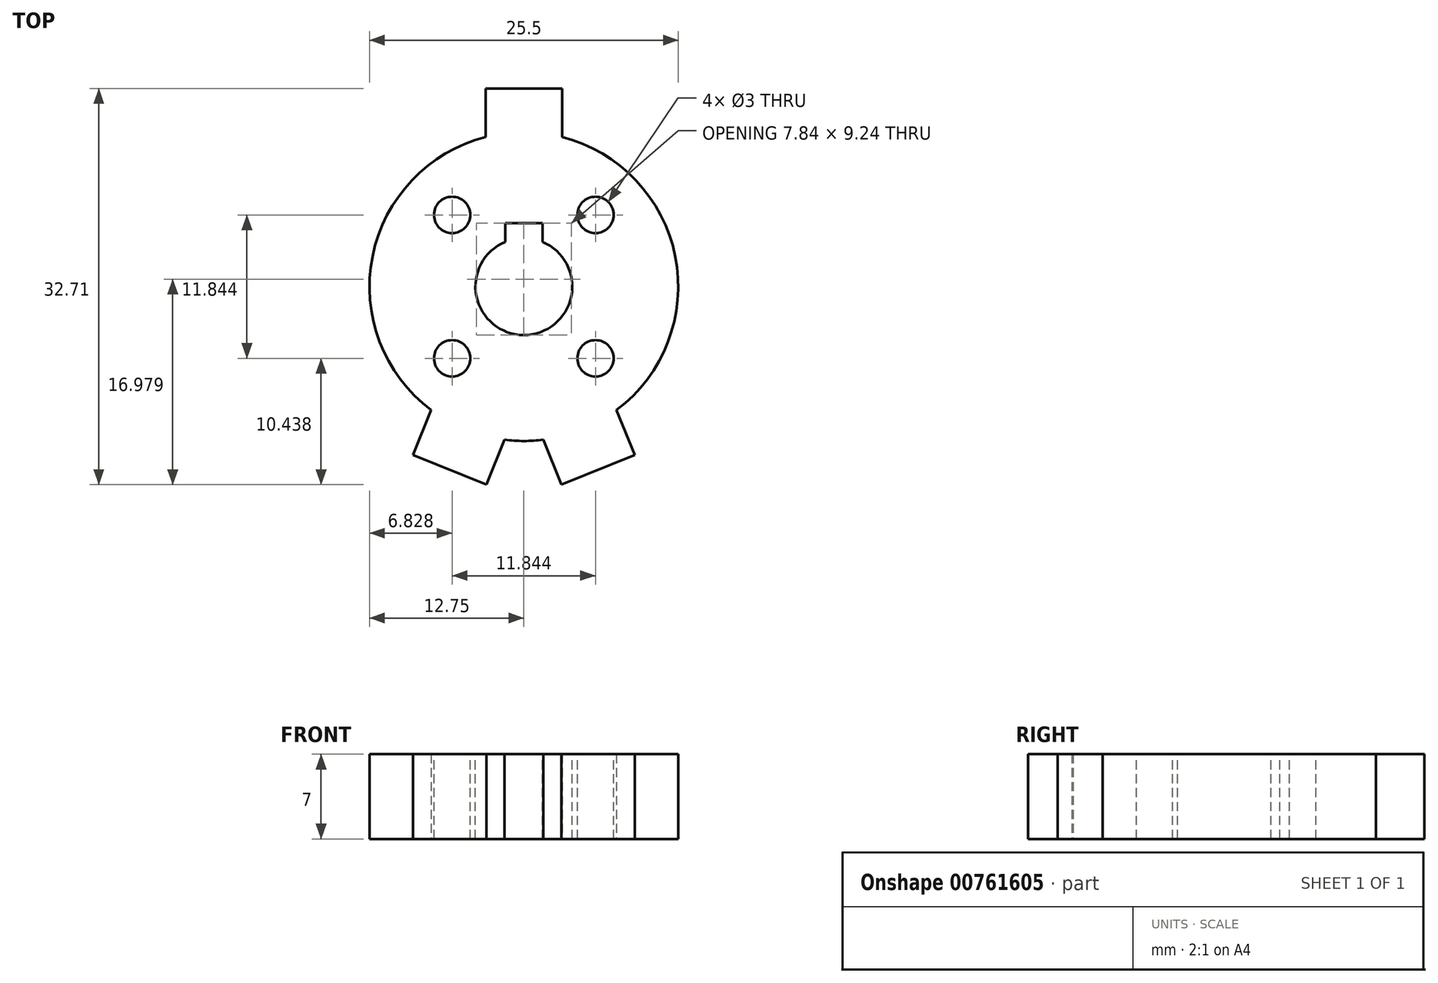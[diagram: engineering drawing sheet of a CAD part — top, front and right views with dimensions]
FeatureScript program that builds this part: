
annotation { "Feature Type Name" : "Feature", "Feature Type Description" : "" }
export const myFeature = defineFeature(function(context is Context, id is Id, definition is map)
    precondition{}
    {
        {
            var Q0;
            Q0=qCreatedBy(makeId("Top.planeOp"),FACE);
            var sketch = newSketch(context, id + "F0", { "sketchPlane" : qUnion([Q0])});
            skArc(sketch, "E0", {"start": v(7.65, -10.2) * mm, "mid": v(12.5, 2.5) * mm, "end": v(3.15, 12.35) * mm});
            skLineSegment(sketch, "E1", {"start": v(0, 12.75) * mm, "end": v(0, -12.75) * mm, "construction": true});
            skLineSegment(sketch, "E2", {"start": v(-3.15, 16.35) * mm, "end": v(0, 16.35) * mm});
            skLineSegment(sketch, "E3", {"start": v(0, 16.35) * mm, "end": v(3.15, 16.35) * mm});
            skLineSegment(sketch, "E4", {"start": v(-3.15, 16.35) * mm, "end": v(-3.15, 12.35) * mm});
            skLineSegment(sketch, "E5", {"start": v(3.15, 16.35) * mm, "end": v(3.15, 12.35) * mm});
            skLineSegment(sketch, "E6", {"start": v(1.6, -12.65) * mm, "end": v(7.65, -10.2) * mm, "construction": true});
            skLineSegment(sketch, "E7", {"start": v(1.6, -12.65) * mm, "end": v(3.1, -16.36) * mm});
            skLineSegment(sketch, "E8", {"start": v(7.65, -10.2) * mm, "end": v(9.15, -13.9) * mm});
            skLineSegment(sketch, "E9", {"start": v(3.1, -16.36) * mm, "end": v(9.15, -13.9) * mm});
            skLineSegment(sketch, "E10.MirrorCS", {"start": v(-1.6, -12.65) * mm, "end": v(-3.1, -16.36) * mm});
            skLineSegment(sketch, "E11.MirrorCS", {"start": v(-3.1, -16.36) * mm, "end": v(-9.15, -13.9) * mm});
            skLineSegment(sketch, "E12.MirrorCS", {"start": v(-7.65, -10.2) * mm, "end": v(-9.15, -13.9) * mm});
            skArc(sketch, "E13.trimOffspring", {"start": v(-1.6, -12.65) * mm, "mid": v(0, -12.75) * mm, "end": v(1.6, -12.65) * mm});
            skArc(sketch, "E14.trimOffspring", {"start": v(-3.15, 12.35) * mm, "mid": v(-12.5, 2.5) * mm, "end": v(-7.65, -10.2) * mm});
            skLineSegment(sketch, "E15", {"start": v(-1.6, -12.65) * mm, "end": v(1.6, -12.65) * mm, "construction": true});
            skLineSegment(sketch, "E16", {"start": v(-3.1, -16.36) * mm, "end": v(3.1, -16.36) * mm, "construction": true});
            skLineSegment(sketch, "E17", {"start": v(-9.15, -13.9) * mm, "end": v(9.15, -13.9) * mm, "construction": true});
            skLineSegment(sketch, "E18", {"start": v(-7.65, -10.2) * mm, "end": v(7.65, -10.2) * mm, "construction": true});
            skSolve(sketch);
        }
        {
            var Q0;
            Q0 = qSketchRegion(id + "F0", true);
            extrude(context, id + "F1", {"entities" : qUnion([Q0]), "depth" : 7 * mm, "offsetDistance" : 25 * mm});
        }
        {
            var Q0;
            Q0=makeQuery(id+"F1.opExtrude","CAP_FACE",FACE,{"disambiguationData":[OSD([sQuery(id+"F0.wireOp",EDGE,"E0"),sQuery(id+"F0.wireOp",EDGE,"E2"),sQuery(id+"F0.wireOp",EDGE,"E3"),sQuery(id+"F0.wireOp",EDGE,"E4"),sQuery(id+"F0.wireOp",EDGE,"E5"),sQuery(id+"F0.wireOp",EDGE,"E7"),sQuery(id+"F0.wireOp",EDGE,"E8"),sQuery(id+"F0.wireOp",EDGE,"E9"),sQuery(id+"F0.wireOp",EDGE,"E10.MirrorCS"),sQuery(id+"F0.wireOp",EDGE,"E11.MirrorCS"),sQuery(id+"F0.wireOp",EDGE,"E12.MirrorCS"),sQuery(id+"F0.wireOp",EDGE,"E13.trimOffspring"),sQuery(id+"F0.wireOp",EDGE,"E14.trimOffspring")])],"isStart":false});
            var sketch = newSketch(context, id + "F2", { "sketchPlane" : qUnion([Q0])});
            skArc(sketch, "E19", {"start": v(-1.55, 3.69) * mm, "mid": v(0, -4) * mm, "end": v(1.55, 3.69) * mm});
            skLineSegment(sketch, "E20", {"start": v(0, 4) * mm, "end": v(0, 5.24) * mm, "construction": true});
            skLineSegment(sketch, "E21", {"start": v(0, 5.24) * mm, "end": v(1.55, 5.24) * mm});
            skLineSegment(sketch, "E22", {"start": v(0, 5.24) * mm, "end": v(-1.55, 5.24) * mm});
            skLineSegment(sketch, "E23", {"start": v(1.55, 5.24) * mm, "end": v(1.55, 3.69) * mm});
            skLineSegment(sketch, "E24", {"start": v(-1.55, 5.24) * mm, "end": v(-1.55, 3.69) * mm});
            skLineSegment(sketch, "E25", {"start": v(-12.75, 0) * mm, "end": v(0, 0) * mm, "construction": true});
            skLineSegment(sketch, "E26", {"start": v(0, 0) * mm, "end": v(-2.83, 2.83) * mm, "construction": true});
            skLineSegment(sketch, "E27", {"start": v(0, 0) * mm, "end": v(8.84, -8.84) * mm, "construction": true});
            skLineSegment(sketch, "E28.MirrorCS", {"start": v(0, 0) * mm, "end": v(8.84, 8.84) * mm, "construction": true});
            skLineSegment(sketch, "E29.MirrorCS", {"start": v(0, 0) * mm, "end": v(-9.02, -9.02) * mm, "construction": true});
            skCircle(sketch, "E30", {"center": v(-5.92, 5.92) * mm, "radius": 1.5 * mm});
            skCircle(sketch, "E31.1.0", {"center": v(-5.92, -5.92) * mm, "radius": 1.5 * mm});
            skCircle(sketch, "E31.2.0", {"center": v(5.92, -5.92) * mm, "radius": 1.5 * mm});
            skCircle(sketch, "E31.3.0", {"center": v(5.92, 5.92) * mm, "radius": 1.5 * mm});
            skLineSegment(sketch, "E32", {"start": v(-2.83, 2.83) * mm, "end": v(-9.02, 9.02) * mm, "construction": true});
            skSolve(sketch);
        }
        {
            var Q0;
            Q0 = qSketchRegion(id + "F2", true);
            var Q1;
            Q1=makeQuery(id+"F1.opExtrude","CAP_FACE",FACE,{"disambiguationData":[OSD([sQuery(id+"F0.wireOp",EDGE,"E0"),sQuery(id+"F0.wireOp",EDGE,"E2"),sQuery(id+"F0.wireOp",EDGE,"E3"),sQuery(id+"F0.wireOp",EDGE,"E4"),sQuery(id+"F0.wireOp",EDGE,"E5"),sQuery(id+"F0.wireOp",EDGE,"E7"),sQuery(id+"F0.wireOp",EDGE,"E8"),sQuery(id+"F0.wireOp",EDGE,"E9"),sQuery(id+"F0.wireOp",EDGE,"E10.MirrorCS"),sQuery(id+"F0.wireOp",EDGE,"E11.MirrorCS"),sQuery(id+"F0.wireOp",EDGE,"E12.MirrorCS"),sQuery(id+"F0.wireOp",EDGE,"E13.trimOffspring"),sQuery(id+"F0.wireOp",EDGE,"E14.trimOffspring")])],"isStart":true});
            extrude(context, id + "F3", {"entities" : qUnion([Q0]), "operationType" : NewBodyOperationType.REMOVE, "endBound" : BoundingType.UP_TO_SURFACE, "oppositeDirection" : true, "depth" : 25 * mm, "endBoundEntityFace" : qUnion([Q1]), "offsetDistance" : 25 * mm});
        }
    });
